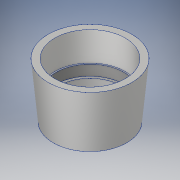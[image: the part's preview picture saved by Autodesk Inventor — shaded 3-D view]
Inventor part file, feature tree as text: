
AUTODESK INVENTOR PART (.ipt)
format: ipt  version: 2017 SP1 (Build 210196100, 196)  size: 161,792 bytes
history: native  units: in
note: dims shown in document units (in); Inventor stores cm internally (conversion verified against a paired STEP export)
features: revolve x1, thread x1, sketch x1
ambient origin geometry x8: Origin, YZ Plane, XZ Plane, XY Plane, X Axis, Y Axis, Z Axis, Center Point
bodies: Body1 (feature_tree)
feature tree (3):
  revolve  "Revolution2"  [1 undecoded]
  thread  "Thread1"  [1 undecoded]
  sketch  "Sketch1"  dims[d0=0.5in d1=1.13in d3=15.0deg d4=0.25in d9=1.5in d11=0.5in d13=3.75in d14=0.25in d15=1.0in d16=0.25in d17=0.5in d18=0.234in d19=0.234in d20=0.5in d22=4.25in d23=2.5in d25=1.0in d26=0.25in d27=5.25in d28=0.125in d29=4.0in d30=0.25in d31=0.1718in d32=1.75in d33=0.125in d34=0.801in d35=0.375in d38=1.0in d40=0.125in d41=90.0deg d42=1.0in d43=0.0in]
note: 2 required parameter values undecoded (feature->parameter linkage not recoverable at this tier; creation-order binding heuristic only, values carry confidence <= 0.55)